# Revit family: Magnuson-Bambu-Coat_Tree-
name_source: partatom
category: Furniture
revit_build: Autodesk Revit 2016 (Build: 20150220_1215(x64)
units: mm (PartAtom-declared; Revit-internal decimal feet)

## family parameters
Always vertical = Yes
Cut with Voids When Loaded = No
Room Calculation Point = No
Shared = No
Work Plane-Based = No

## types (2) — shared parameters
Assembly Code = E2020200
Base Finish = MAG-Paint Steel White
Diameter = 14 1/2"
Glide Finish = MAG-Plastic Black
Height = 67 11/16"
Hook Finish = MAG-Plastic Black
Keynote = 12500
Low Emitting Finish = Yes
Low Emitting Material = Yes
Manufacturer = Magnuson Group
Post Finish = MAG-Paint Steel White
Revit File Built By = https://servex-us.com
Salvage or Reuse = Yes
Type Comments = Bambu
URL = https://magnusongroup.com
Umbrella Finish = MAG-Paint Steel White
zero-valued in all types: Percentage of Recycled Content

## per-type parameters (varying)
| type | Description | Hook 3 | Umbrella Holder |
| BAMBU-03 | Coat tree with 6 molded plastic hooks. Includes umbrella holder. | No | Yes |
| BAMBU-01 | Coat tree with 9 molded plastic hooks. | Yes | No |

note: column(s) folded — value = type name in every type: Model

## geometry (parser evidence)
native form markers: Sweep x2
no freeform markers — native parametric forms only
